# Revit family: IS_Idealrain_B9419_BIM_DE
name_source: partatom
category: Plumbing Fixtures
revit_build: Autodesk Revit MEP 2016 (Build: 20161004_0715(x64)
units: mm (PartAtom-declared; Revit-internal decimal feet)

## family parameters
Always vertical = No
Cut with Voids When Loaded = No
OmniClass Number = 23.45.05.14.17.17
OmniClass Title = Group Showers
Part Type = Normal
Room Calculation Point = No
Round Connector Dimension = Use Diameter
Shared = No
Work Plane-Based = No

## types (1)
- B9419AA IDEALRAIN shower kit with 3 function 100mm handspray, 720mm slide rail
    Accessories = www.idealstandard.de\ersatzteile
    AssetType = Fixed
    BIMObjectName = ISI_IdealStandard_ShowerFittingsPackage_IDEALRAIN_B9419AA
    BIMobject category = Showers
    BOSUseNativeGeometries = 1
    BarCode = 3800861024101
    Brand = Ideal Standard
    Brand url = http://www.idealstandard.de
    CodePerformance = 0
    Color = Chrome
    ConnectionType = Plumbing
    Cost = 0 $
    CurrencyUnit = €
    CurrentRevision = 1
    Date of publishing = 42828
    Description = B9419AA IDEALRAIN shower kit with 3 function 100mm handspray, 720mm slide rail
    DurationUnit = Jaar
    EAN code = https://3800861024101
    Edition number = 1
    ExpectedLife = 25
    FaucetType = pillar
    Features = IDEALRAIN shower kit with 3 function 100mm handspray, 720mm slide rail
    Finish = Chrome
    IFC Classification = Valve
    IfcExportAs = Sanitary terminal type
    IfcExportType = BRASSWARE SHOWER
    Installation instructions = http://www.idealstandard.de
    InstallationInstructions = www.idealstandard.de\produkte
    LinearUnits = millimetres
    MainColor = Chrome
    MaintenanceInformation = www.idealstandard.de
    Manufacturer = http://www.idealstandard.de
    Manufacturer name = Ideal Standard
    ManufacturerURL = http://www.idealstandard.de
    Material = Brass
    Material main = Brass
    Model = B9419AA
    ModelNumber = B9419AA
    ModelReference = B9419AA IDEALRAIN shower kit with 3 function 100mm handspray, 720mm slide rail
    NBS Reference Code = 35-06-81
    NBS Reference Description = Shower Heads
    Name = ISI_IdealStandard_ShowerFittingsPackage_IDEALRAIN_B9419AA
    NettWeight = 1,095 kg
    Nominal height = 0
    Nominal width = 0
    NominalHeight = 723 mm
    NominalLength = 183 mm
    NominalWidth = 164 mm
    OmniClass Code = 23-31 11 00
    OmniClass Description = Faucets
    Product Guid = ba32da01-6997-4b30-9ac8-91d1cfeb10f4
    Product SKU = B9419
    Product certification = 0
    Product data url = https://bimobject.com
    Product family = IDEALRAIN
    Product group = Shower
    Product name = IDEALRAIN shower kit with 3 function 100mm handspray, 720mm slide rail
    Product url = http://www.idealstandard.de
    ProductInformation = www.idealstandard.de/produkte
    QR code = http://bimobject.com
    Shape = Sculptured
    Size = 723x183x164 mm
    Space = Internal
    SpareParts = www.idealstandard.de/ersatzteile
    Technical description = http://www.idealstandard.de
    TestPressure = 10 Bar
    URL = http://www.idealstandard.de
    Uniclass 2.0 Code = PR-35-06-81
    Uniclass 2.0 Description = Shower Heads
    Uniclass 2015 Code = Pr_40_20_87_76
    Uniclass 2015 Name = Shower heads
    Uniclass2015Code = Pr_40_20_87_75
    Uniclass2015Title = Shower fittings package
    Uniclass2015Version = Products v1.1
    VolumeUnits = Litres
    Weight Net (Kg) = 1.1
    WorkingPressure = 1-5 Bar

## geometry (parser evidence)
native form markers: Blend x2, Sweep x2
no freeform markers — native parametric forms only
